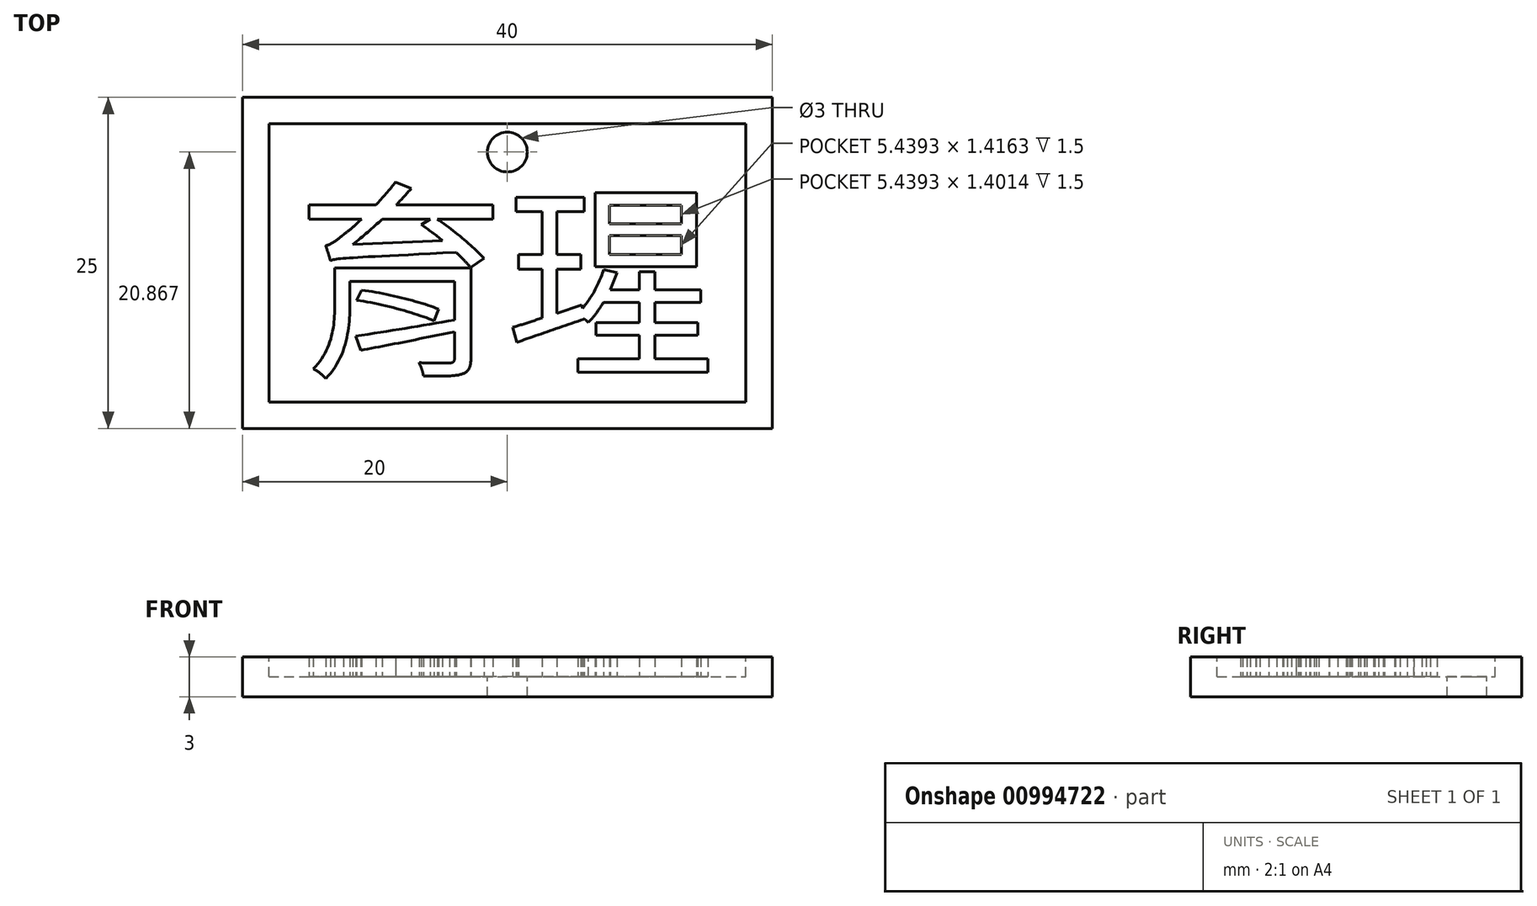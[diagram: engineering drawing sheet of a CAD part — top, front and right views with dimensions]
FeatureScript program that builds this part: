
annotation { "Feature Type Name" : "Feature", "Feature Type Description" : "" }
export const myFeature = defineFeature(function(context is Context, id is Id, definition is map)
    precondition{}
    {
        {
            var Q0;
            Q0=qCreatedBy(makeId("Top.planeOp"),FACE);
            var sketch = newSketch(context, id + "F0", { "sketchPlane" : qUnion([Q0])});
            skLineSegment(sketch, "E0.bottom", {"start": v(20, -12.5) * mm, "end": v(-20, -12.5) * mm});
            skLineSegment(sketch, "E0.top", {"start": v(20, 12.5) * mm, "end": v(-20, 12.5) * mm});
            skLineSegment(sketch, "E0.left", {"start": v(20, -12.5) * mm, "end": v(20, 12.5) * mm});
            skLineSegment(sketch, "E0.right", {"start": v(-20, -12.5) * mm, "end": v(-20, 12.5) * mm});
            skPoint(sketch, "E0.middle", {"position": v(0, 0) * mm});
            skSolve(sketch);
        }
        {
            var Q0;
            Q0=makeQuery(id+"F0.imprint","IMPRINT",FACE,{"disambiguationData":[TD([[makeQuery(id+"F0.imprint","IMPRINT",EDGE,{"derivedFrom":sQuery(id+"F0.wireOp",EDGE,"E0.bottom")}),-1.0]])]});
            extrude(context, id + "F1", {"entities" : qUnion([Q0]), "depth" : 3 * mm, "offsetDistance" : 25 * mm});
        }
        {
            var Q0;
            Q0=makeQuery(id+"F1.opExtrude","CAP_FACE",FACE,{"disambiguationData":[OSD([sQuery(id+"F0.wireOp",EDGE,"E0.bottom"),sQuery(id+"F0.wireOp",EDGE,"E0.top"),sQuery(id+"F0.wireOp",EDGE,"E0.left"),sQuery(id+"F0.wireOp",EDGE,"E0.right")])],"isStart":false});
            var sketch = newSketch(context, id + "F2", { "sketchPlane" : qUnion([Q0])});
            skLineSegment(sketch, "E1.0", {"start": v(18, -10.5) * mm, "end": v(18, 10.5) * mm});
            skLineSegment(sketch, "E1.1", {"start": v(-18, -10.5) * mm, "end": v(18, -10.5) * mm});
            skLineSegment(sketch, "E1.2", {"start": v(-18, 10.5) * mm, "end": v(-18, -10.5) * mm});
            skLineSegment(sketch, "E1.3", {"start": v(18, 10.5) * mm, "end": v(-18, 10.5) * mm});
            skSolve(sketch);
        }
        {
            var Q0;
            Q0=makeQuery(id+"F2.imprint","IMPRINT",FACE,{"disambiguationData":[TD([[makeQuery(id+"F2.imprint","IMPRINT",EDGE,{"derivedFrom":sQuery(id+"F2.wireOp",EDGE,"E1.0")}),1.0]])]});
            extrude(context, id + "F3", {"entities" : qUnion([Q0]), "operationType" : NewBodyOperationType.REMOVE, "oppositeDirection" : true, "depth" : 1.5 * mm, "offsetDistance" : 25 * mm});
        }
        {
            var Q0;
            Q0=makeQuery(id+"F3.boolean.opBoolean","COPY",FACE,{"derivedFrom":makeQuery(id+"F3.opExtrude","CAP_FACE",FACE,{"disambiguationData":[OSD([sQuery(id+"F2.wireOp",EDGE,"E1.0"),sQuery(id+"F2.wireOp",EDGE,"E1.1"),sQuery(id+"F2.wireOp",EDGE,"E1.2"),sQuery(id+"F2.wireOp",EDGE,"E1.3")])],"isStart":false})});
            var sketch = newSketch(context, id + "F4", { "sketchPlane" : qUnion([Q0])});
            skCircle(sketch, "E2", {"center": v(0, 8.37) * mm, "radius": 1.5 * mm});
            skSolve(sketch);
        }
        {
            var Q0;
            Q0=makeQuery(id+"F4.imprint","IMPRINT",FACE,{"disambiguationData":[TD([[makeQuery(id+"F4.imprint","IMPRINT",EDGE,{"derivedFrom":sQuery(id+"F4.wireOp",EDGE,"E2")}),1.0]])]});
            var Q1;
            Q1=sQuery(id+"F4.wireOp",EDGE,"E2");
            extrude(context, id + "F5", {"entities" : qUnion([Q0]), "operationType" : NewBodyOperationType.REMOVE, "surfaceEntities" : qUnion([Q1]), "oppositeDirection" : true, "depth" : 1.5 * mm, "offsetDistance" : 25 * mm});
        }
        {
            var Q0;
            Q0=makeQuery(id+"F3.boolean.opBoolean","COPY",FACE,{"derivedFrom":makeQuery(id+"F3.opExtrude","CAP_FACE",FACE,{"disambiguationData":[OSD([sQuery(id+"F2.wireOp",EDGE,"E1.0"),sQuery(id+"F2.wireOp",EDGE,"E1.1"),sQuery(id+"F2.wireOp",EDGE,"E1.2"),sQuery(id+"F2.wireOp",EDGE,"E1.3")])],"isStart":false})});
            var sketch = newSketch(context, id + "F6", { "sketchPlane" : qUnion([Q0])});
            skText(sketch, "E3", { "text": "育瑆", "fontName": "NotoSansCJKtc-Regular.otf"});
            const initialGuessF6  = {"E3": [-0.016, -0.00739, 1, 0, 0.01145]};
            skSetInitialGuess(sketch, initialGuessF6);
            skSolve(sketch);
        }
        {
            var Q0;
            Q0 = qSketchRegion(id + "F6", true);
            extrude(context, id + "F7", {"entities" : qUnion([Q0]), "operationType" : NewBodyOperationType.ADD, "depth" : 1.5 * mm, "offsetDistance" : 25 * mm});
        }
    });
